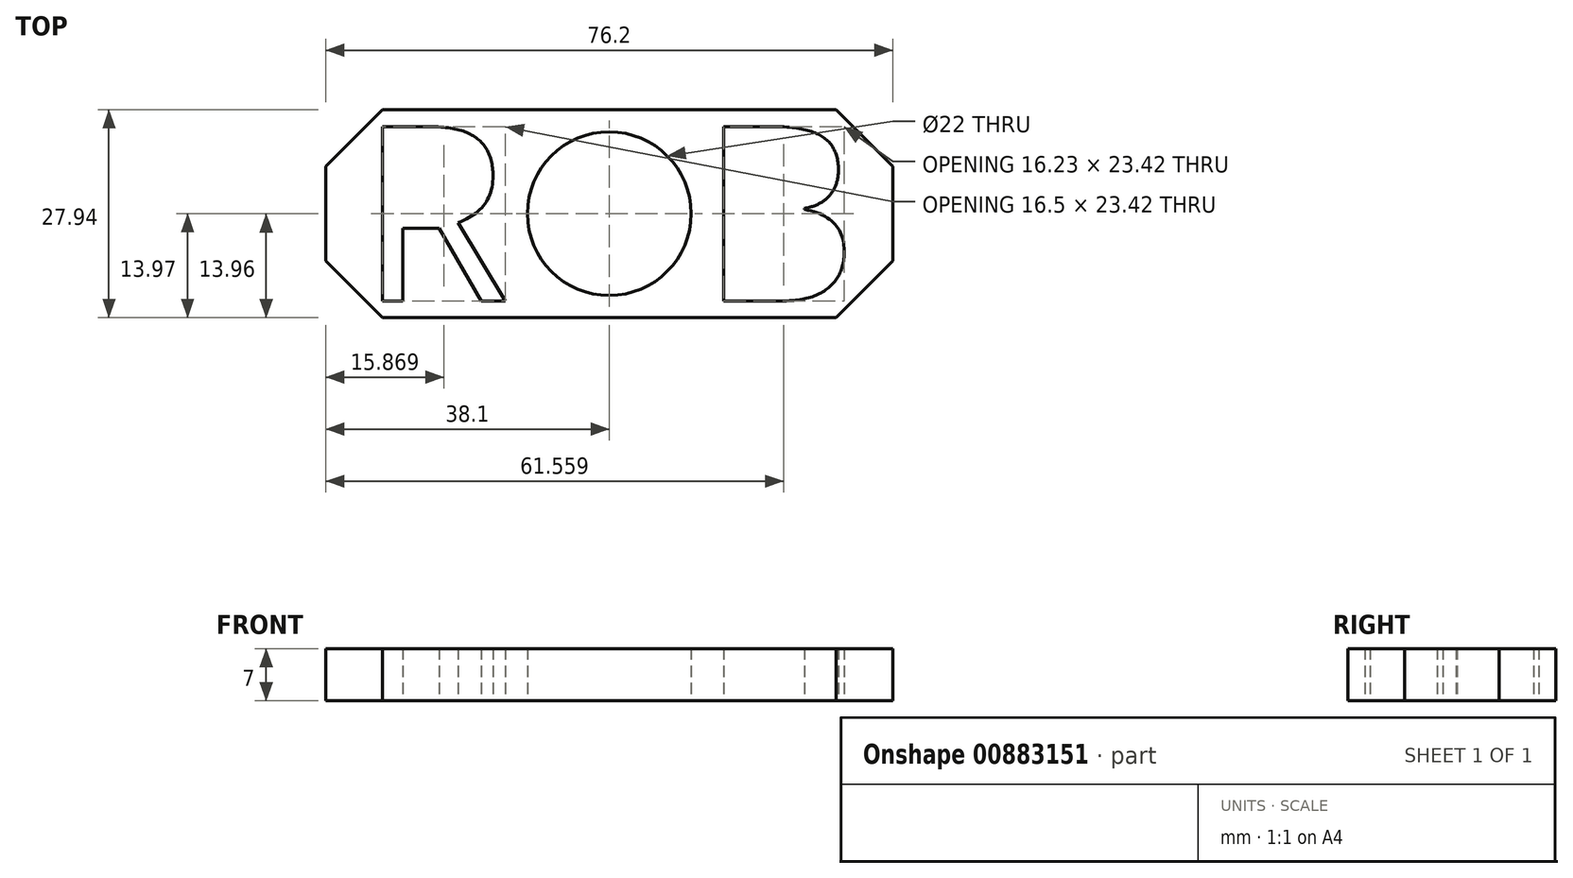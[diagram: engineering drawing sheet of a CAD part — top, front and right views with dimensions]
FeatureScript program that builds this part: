
annotation { "Feature Type Name" : "Feature", "Feature Type Description" : "" }
export const myFeature = defineFeature(function(context is Context, id is Id, definition is map)
    precondition{}
    {
        {
            var Q0;
            Q0=qCreatedBy(makeId("Top.planeOp"),FACE);
            var sketch = newSketch(context, id + "F0", { "sketchPlane" : qUnion([Q0])});
            skCircle(sketch, "E0", {"center": v(0, 0) * mm, "radius": 11 * mm});
            skLineSegment(sketch, "E1.bottom", {"start": v(-38.1, -13.97) * mm, "end": v(38.1, -13.97) * mm});
            skLineSegment(sketch, "E1.top", {"start": v(-38.1, 13.97) * mm, "end": v(38.1, 13.97) * mm});
            skLineSegment(sketch, "E1.left", {"start": v(-38.1, -13.97) * mm, "end": v(-38.1, 13.97) * mm});
            skLineSegment(sketch, "E1.right", {"start": v(38.1, -13.97) * mm, "end": v(38.1, 13.97) * mm});
            skText(sketch, "E2", { "text": "ROB", "fontName": "OpenSans-Regular.ttf"});
            const initialGuessF0  = {"E2": [-0.0337, -0.01172, 1, 0, 0.02362]};
            skSetInitialGuess(sketch, initialGuessF0);
            skSolve(sketch);
        }
        {
            var Q0;
            Q0=makeQuery(id+"F0.imprint","IMPRINT",FACE,{"disambiguationData":[TD([[makeQuery(id+"F0.imprint","IMPRINT",EDGE,{"derivedFrom":sQuery(id+"F0.wireOp",EDGE,"E1.bottom")}),1.0]])]});
            var Q1;
            {var subQ0=sQuery(id+"F0.wireOp",EDGE,"E2.sketch_text.stroke-19");Q1=makeQuery(id+"F0.imprint","IMPRINT",FACE,{"disambiguationData":[TD([[makeQuery(id+"F0.imprint","IMPRINT",EDGE,{"derivedFrom":subQ0}),-1.0]])]});}
            extrude(context, id + "F1", {"entities" : qUnion([Q0, Q1]), "depth" : 7 * mm, "offsetDistance" : 25.4 * mm});
        }
        {
            var Q0;
            Q0=makeQuery(id+"F1.opExtrude","SWEPT_EDGE",EDGE,{"disambiguationData":[OSD([sQuery(id+"F0.wireOp",EDGE,"E1.bottom"),sQuery(id+"F0.wireOp",EDGE,"E1.left")])]});
            var Q1;
            Q1=makeQuery(id+"F1.opExtrude","SWEPT_EDGE",EDGE,{"disambiguationData":[OSD([sQuery(id+"F0.wireOp",EDGE,"E1.top"),sQuery(id+"F0.wireOp",EDGE,"E1.left")])]});
            var Q2;
            Q2=makeQuery(id+"F1.opExtrude","SWEPT_EDGE",EDGE,{"disambiguationData":[OSD([sQuery(id+"F0.wireOp",EDGE,"E1.bottom"),sQuery(id+"F0.wireOp",EDGE,"E1.right")])]});
            var Q3;
            Q3=makeQuery(id+"F1.opExtrude","SWEPT_EDGE",EDGE,{"disambiguationData":[OSD([sQuery(id+"F0.wireOp",EDGE,"E1.top"),sQuery(id+"F0.wireOp",EDGE,"E1.right")])]});
            chamfer(context, id + "F2", {"entities" : qUnion([Q0, Q1, Q2, Q3]), "width" : 7.62 * mm, "tangentPropagation" : true});
        }
    });
